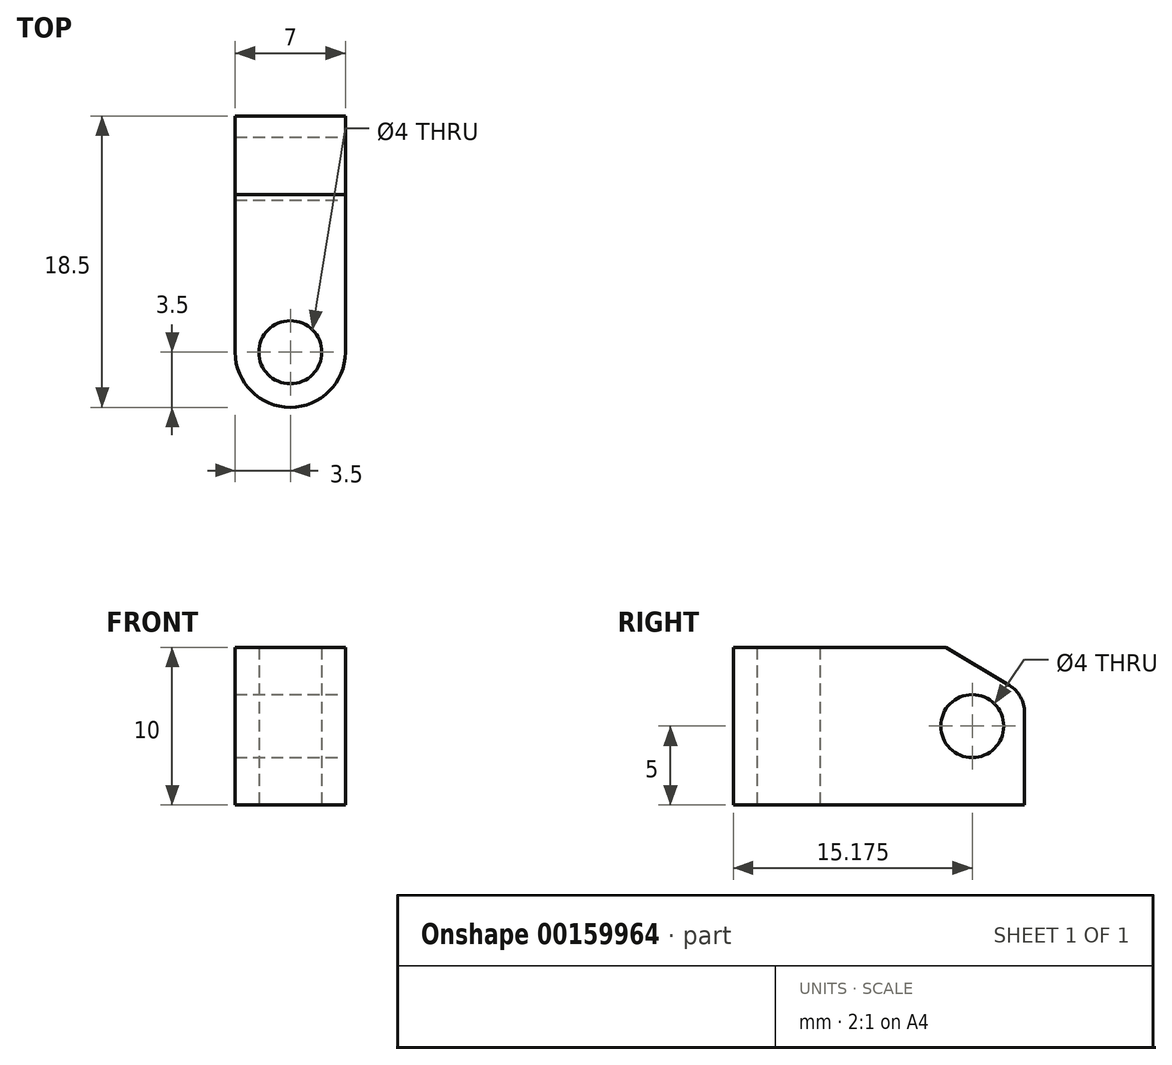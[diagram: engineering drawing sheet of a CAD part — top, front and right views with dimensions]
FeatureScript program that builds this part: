
annotation { "Feature Type Name" : "Feature", "Feature Type Description" : "" }
export const myFeature = defineFeature(function(context is Context, id is Id, definition is map)
    precondition{}
    {
        {
            var Q0;
            Q0=qCreatedBy(makeId("Top.planeOp"),FACE);
            var sketch = newSketch(context, id + "F0", { "sketchPlane" : qUnion([Q0])});
            skArc(sketch, "E0", {"start": v(-3.5, 0) * mm, "mid": v(0, -3.5) * mm, "end": v(3.5, 0) * mm});
            skCircle(sketch, "E1", {"center": v(0, 0) * mm, "radius": 2 * mm});
            skLineSegment(sketch, "E2", {"start": v(-3.5, 0) * mm, "end": v(-3.5, 15) * mm});
            skLineSegment(sketch, "E3", {"start": v(-3.5, 15) * mm, "end": v(3.5, 15) * mm});
            skLineSegment(sketch, "E4", {"start": v(3.5, 0) * mm, "end": v(3.5, 15) * mm});
            skSolve(sketch);
        }
        {
            var Q0;
            Q0=makeQuery(id+"F0.imprint","IMPRINT",FACE,{"disambiguationData":[TD([[makeQuery(id+"F0.imprint","IMPRINT",EDGE,{"derivedFrom":sQuery(id+"F0.wireOp",EDGE,"E0")}),1.0]])]});
            extrude(context, id + "F1", {"entities" : qUnion([Q0]), "depth" : 10 * mm});
        }
        {
            var Q0;
            Q0=makeQuery(id+"F1.opExtrude","SWEPT_FACE",FACE,{"disambiguationData":[OSD([sQuery(id+"F0.wireOp",EDGE,"E4")])]});
            var sketch = newSketch(context, id + "F2", { "sketchPlane" : qUnion([Q0])});
            skCircle(sketch, "E5", {"center": v(11.68, 5) * mm, "radius": 2 * mm});
            skLineSegment(sketch, "E6", {"start": v(15, 5) * mm, "end": v(15, 5) * mm});
            skPoint(sketch, "E7.visualSharp", {"position": v(15, 10) * mm});
            skPoint(sketch, "E8.visualSharp", {"position": v(15, 0) * mm});
            skLineSegment(sketch, "E9", {"start": v(10, 10) * mm, "end": v(15, 10) * mm});
            skLineSegment(sketch, "E10", {"start": v(15, 5) * mm, "end": v(15, 5.87) * mm});
            skLineSegment(sketch, "E11", {"start": v(15, 4.13) * mm, "end": v(15, 5) * mm});
            skLineSegment(sketch, "E12", {"start": v(10, 0) * mm, "end": v(15, 0) * mm});
            skPoint(sketch, "E13.orphan", {"position": v(8.35, 5) * mm});
            skLineSegment(sketch, "E14", {"start": v(10, 10) * mm, "end": v(14.03, 7.58) * mm});
            skLineSegment(sketch, "E15", {"start": v(14.03, 2.41) * mm, "end": v(10, 0) * mm});
            skArc(sketch, "E16.filletArc", {"start": v(15, 5.87) * mm, "mid": v(14.74, 6.85) * mm, "end": v(14.03, 7.58) * mm});
            skArc(sketch, "E17.filletArc", {"start": v(14.03, 2.41) * mm, "mid": v(14.74, 3.14) * mm, "end": v(15, 4.13) * mm});
            skSolve(sketch);
        }
        {
            var Q0;
            Q0=makeQuery(id+"F2.imprint","IMPRINT",FACE,{"disambiguationData":[TD([[makeQuery(id+"F2.imprint","IMPRINT",EDGE,{"derivedFrom":sQuery(id+"F2.wireOp",EDGE,"E7.filletArc")}),-1.0]])]});
            var Q1;
            Q1=makeQuery(id+"F2.imprint","IMPRINT",FACE,{"disambiguationData":[TD([[makeQuery(id+"F2.imprint","IMPRINT",EDGE,{"derivedFrom":sQuery(id+"F2.wireOp",EDGE,"E8.filletArc")}),-1.0]])]});
            var Q2;
            Q2=makeQuery(id+"F2.imprint","IMPRINT",FACE,{"disambiguationData":[TD([[makeQuery(id+"F2.imprint","IMPRINT",EDGE,{"derivedFrom":sQuery(id+"F2.wireOp",EDGE,"E5")}),1.0]])]});
            var Q3;
            Q3=makeQuery(id+"F2.imprint","IMPRINT",FACE,{"disambiguationData":[TD([[makeQuery(id+"F2.imprint","IMPRINT",EDGE,{"derivedFrom":sQuery(id+"F2.wireOp",EDGE,"E9")}),-1.0]])]});
            extrude(context, id + "F3", {"entities" : qUnion([Q0, Q1, Q2, Q3]), "operationType" : NewBodyOperationType.REMOVE, "oppositeDirection" : true, "depth" : 25 * mm});
        }
    });
